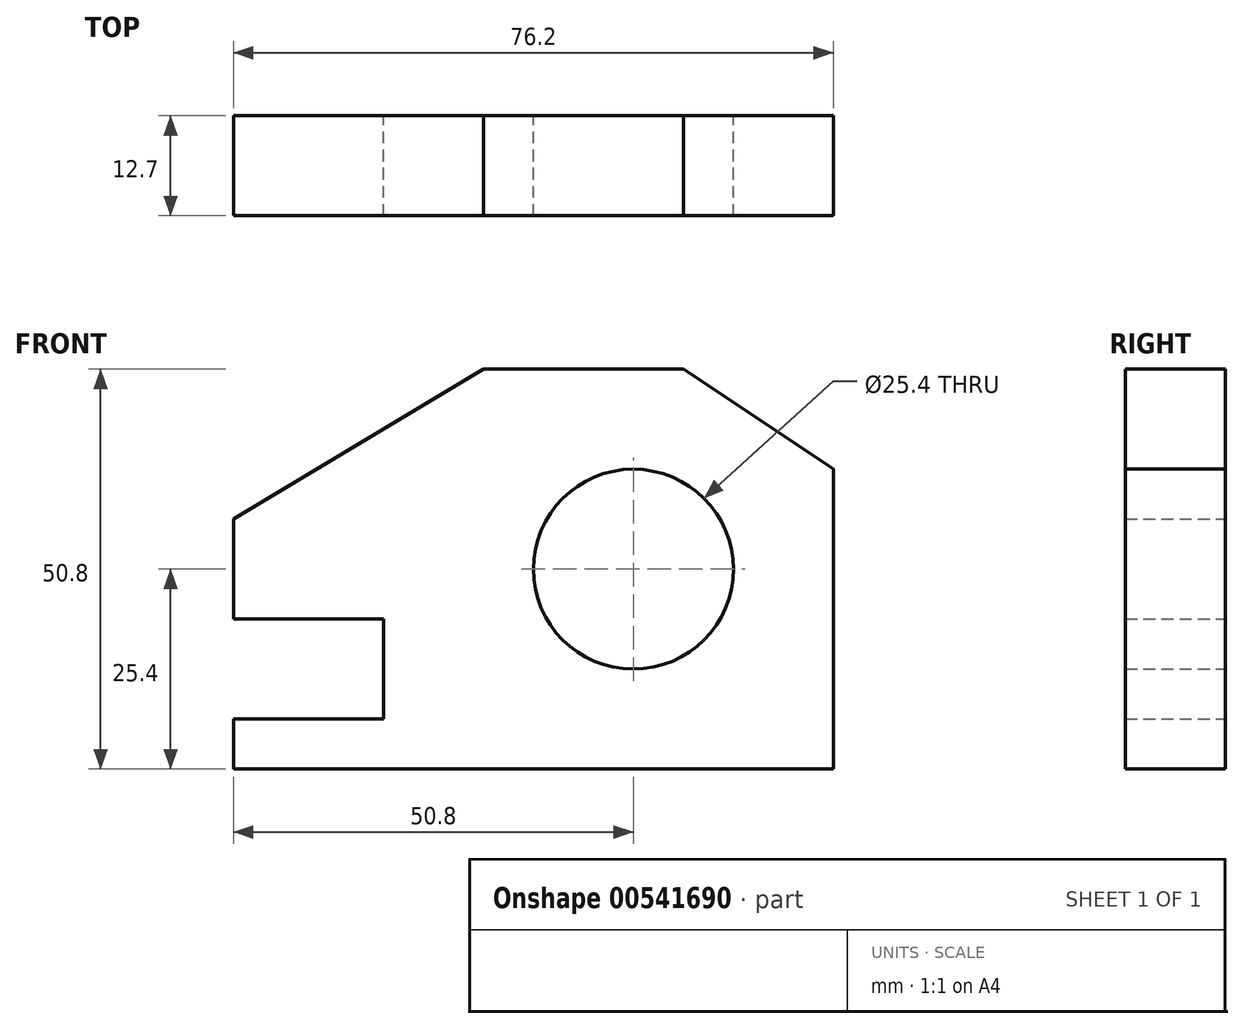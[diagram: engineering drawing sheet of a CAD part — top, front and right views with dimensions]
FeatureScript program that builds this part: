
annotation { "Feature Type Name" : "Feature", "Feature Type Description" : "" }
export const myFeature = defineFeature(function(context is Context, id is Id, definition is map)
    precondition{}
    {
        {
            var Q0;
            Q0=qCreatedBy(makeId("Front.planeOp"),FACE);
            var sketch = newSketch(context, id + "F0", { "sketchPlane" : qUnion([Q0])});
            skLineSegment(sketch, "E0", {"start": v(0, 0) * mm, "end": v(76.2, 0) * mm});
            skLineSegment(sketch, "E1", {"start": v(76.2, 0) * mm, "end": v(76.2, 38.1) * mm});
            skLineSegment(sketch, "E2", {"start": v(76.2, 38.1) * mm, "end": v(57.15, 50.8) * mm});
            skLineSegment(sketch, "E3", {"start": v(57.15, 50.8) * mm, "end": v(31.75, 50.8) * mm});
            skLineSegment(sketch, "E4", {"start": v(31.75, 50.8) * mm, "end": v(0, 31.75) * mm});
            skLineSegment(sketch, "E5", {"start": v(0, 31.75) * mm, "end": v(0, 19.05) * mm});
            skLineSegment(sketch, "E6", {"start": v(0, 19.05) * mm, "end": v(19.05, 19.05) * mm});
            skLineSegment(sketch, "E7", {"start": v(19.05, 19.05) * mm, "end": v(19.05, 6.35) * mm});
            skLineSegment(sketch, "E8", {"start": v(19.05, 6.35) * mm, "end": v(0, 6.35) * mm});
            skLineSegment(sketch, "E9", {"start": v(0, 6.35) * mm, "end": v(0, 0) * mm});
            skCircle(sketch, "E10", {"center": v(50.8, 25.4) * mm, "radius": 12.7 * mm});
            skSolve(sketch);
        }
        {
            var Q0;
            Q0=makeQuery(id+"F0.imprint","IMPRINT",FACE,{"disambiguationData":[TD([[makeQuery(id+"F0.imprint","IMPRINT",EDGE,{"derivedFrom":sQuery(id+"F0.wireOp",EDGE,"E0")}),1.0]])]});
            extrude(context, id + "F1", {"entities" : qUnion([Q0]), "depth" : 12.7 * mm, "offsetDistance" : 25.4 * mm});
        }
    });
